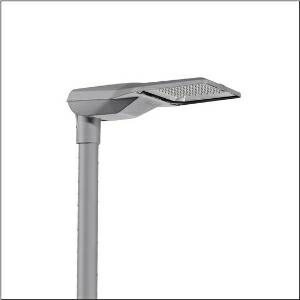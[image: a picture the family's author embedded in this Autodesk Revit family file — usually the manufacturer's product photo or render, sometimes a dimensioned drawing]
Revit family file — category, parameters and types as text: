
# Revit family: streetlight_sl_21_iq_midi___st1_0ab_5xe3m31g08mb_7004
name_source: partatom
category: Lighting Fixtures
units: mm (PartAtom-declared; Revit-internal decimal feet)

## family parameters
Cut with Voids When Loaded = No
Host = Face
Light Source = No
Part Type = Normal
Room Calculation Point = No
Round Connector Dimension = Use Diameter
Shared = No

## types (1)
- --- (1 x LED, 17170 lm, 146.7 W, 3000K)
    Apparent Load = 147 VA
    CIE Flux Codes = 38 73 97 100 100
    Color Rendering = 70
    Color Temperature = 3000K
    Default Elevation = 1800 mm
    Description = Streetlight SL 21 iQ midi, mast luminaire, primary light control with lens, of PMMA, primary optical cover: cover, of toughened safety glass, transparent, light distribution: ST1.0aB, light emission: direct distribution, primary light characteristic: asymmetric, installation type: post-top, side-entry, LED, High Power LED, rated luminous flux: 17.170lm, luminous efficacy: 117lm/W, light colour: 730, colour temperature: 3000K, control gear: iQ Street-Remote, control: Street-Remote, Auto-Match, Temp-Guard, Lumen-Switch, Night-Set, Smart-Wire, Light-Fading, Desk-Remote (wireless, voltage-free reading and setting of iQ features in the workshop via application-optimized NFC function/RFID function), optimised constant luminous flux control (CLO 2.0), pre-setting: linear dimming characteristic, mains connection: 230..240V, AC, 50/60Hz, start of lifetime: 147W, end of service life: 161W, reduction: 62W, luminaire housing, of diecast aluminium, powder-coated, Siteco® metallic grey (DB 702S), corrosivity category C5 mid according to DIN EN ISO 12944, please order mast flange separately, inclination adjustable: 0°, 5°, 10°, 15°, sealing non-destructively replaceable, multi-level sealing system, length: 644mm, width: 335mm, height: 110mm, mast flange for spigot size: 42mm (side-entry): 5XC10008XM4, 60/48mm (side-entry/post-top): 5XC10108XM2, 76/60mm (side-entry/post-top): 5XC10108XM1, mounting height: 4..8m, protection rating (complete): IP66, insulation class (complete): insulation class II (safety insulation), certification: CE, ENEC, ENEC+, VDE, impact resistance: IK10, permissible operating ambient temperature for outdoor applications: -40..+50°C, standard-compliant lighting for roads and squares, packaging unit: 1 piece

Light Distribution: ST1.0aB
    Height = 111 mm
    Lamp = 1 x LED
    Lamp Light Flux = 17170 lm
    Lamp Power = 146.7 W
    Lamp count = 1
    Length = 644 mm
    Luminous efficacy = 117 lm/W
    Manufacturer = Siteco
    ModVariant = No
    Model = 5XE3M31G08MB
    Number of Poles = 1
    OnlyDefault = Yes
    Power Factor = 1
    Product Name = Streetlight SL 21 iQ midi | ST1.0aB
    Product group = mast luminaire | pylon top
    ProductGroupID = 6100
    Protection Class = Protection class II
    Protection Degree = IP 66
    RLX_Detail_Level = 1
    RLX_Emergency_Light_Flux = 0 lm
    RLX_Emergency_Type = 0
    RLX_Emergency_Type_DB = No
    RlxData = <blob elided: 26909 chars, md5=e731034a>
    Socket = socket
    Standby Power = 0 W
    System Light Flux = 17170 lm
    System Power = 147 W
    Type Comments = factory setting: luminous flux: 100 % | dim-lin: 254 | 753 mA
    Type Image = l_1004298.jpg
    URL = http://relux.com
    VarID = @adj_204297
    Voltage = 0 V
    Weight = 0.00 kg
    Width = 336 mm

## geometry (parser evidence)
native form markers: Blend x4, Sweep x10
no freeform markers — native parametric forms only
